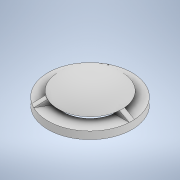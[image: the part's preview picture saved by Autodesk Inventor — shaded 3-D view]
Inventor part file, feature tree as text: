
AUTODESK INVENTOR PART (.ipt)
format: ipt  version: 2022 (Build 260153000, 153)  size: 282,624 bytes
history: native  units: in
note: dims shown in document units (in); Inventor stores cm internally (conversion verified against a paired STEP export)
features: sketch x3, extrude x2, delete_face x2, surface_op x2, revolve x1, pattern_circular x1, other x1
ambient origin geometry x8: Origin, YZ Plane, XZ Plane, XY Plane, X Axis, Y Axis, Z Axis, Center Point
bodies: Solid1 (feature_tree)
feature tree (12):
  extrude  "Extrusion1"  Depth=3.1102in
  revolve  "Revolution1"  Angle=90.0deg
  extrude  "Extrusion5"  Depth=1.1811in TaperAngle=360.0deg
  pattern_circular  "Circular Pattern2"  Count=3  [1 undecoded]
  delete_face  "Delete Face1"
  delete_face  "Delete Face2"
  surface_op  "Stitch Surface1"
  sketch  "Sketch1"  dims[d0=1.9685in d1=3.1102in]
  sketch  "Sketch6"  dims[d2=0.2756in d3=0.0in d25=90.0deg]
  sketch  "Sketch7"  dims[d26=0.1969in d27=0.0in d28=1.1811in d29=360.0deg d42=1.1811in d43=0.7874in d45=0.1969in d46=0.9843in d50=1.378in d51=0.1969in d52=0.1969in d53=0.0in]
  other  "Srf2"
  surface_op  "Boundary Patch1"
note: 1 required parameter value undecoded (feature->parameter linkage not recoverable at this tier; creation-order binding heuristic only, values carry confidence <= 0.55)
